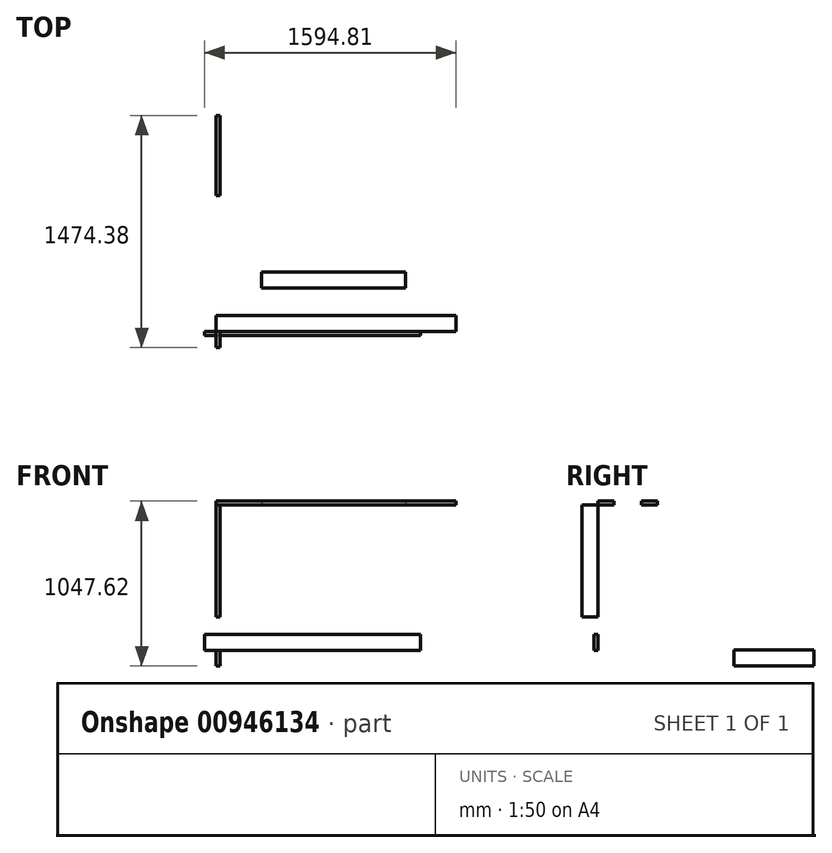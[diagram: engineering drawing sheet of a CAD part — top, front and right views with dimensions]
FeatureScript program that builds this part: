
annotation { "Feature Type Name" : "Feature", "Feature Type Description" : "" }
export const myFeature = defineFeature(function(context is Context, id is Id, definition is map)
    precondition{}
    {
        {
            var Q0;
            Q0=qCreatedBy(makeId("Top.planeOp"),FACE);
            var sketch = newSketch(context, id + "F0", { "sketchPlane" : qUnion([Q0])});
            skLineSegment(sketch, "E0.bottom", {"start": v(0, 0) * mm, "end": v(1524, 0) * mm});
            skLineSegment(sketch, "E0.top", {"start": v(0, 101.6) * mm, "end": v(1524, 101.6) * mm});
            skLineSegment(sketch, "E0.left", {"start": v(0, 0) * mm, "end": v(0, 101.6) * mm});
            skLineSegment(sketch, "E0.right", {"start": v(1524, 0) * mm, "end": v(1524, 101.6) * mm});
            skSolve(sketch);
        }
        {
            var Q0;
            Q0 = qSketchRegion(id + "F0", true);
            extrude(context, id + "F1", {"entities" : qUnion([Q0]), "depth" : 25.4 * mm, "offsetDistance" : 25.4 * mm});
        }
        {
            var Q0;
            Q0=qCreatedBy(makeId("Right.planeOp"),FACE);
            var sketch = newSketch(context, id + "F2", { "sketchPlane" : qUnion([Q0])});
            skLineSegment(sketch, "E1.bottom", {"start": v(0, 0) * mm, "end": v(-101.6, 0) * mm});
            skLineSegment(sketch, "E1.top", {"start": v(0, -711.2) * mm, "end": v(-101.6, -711.2) * mm});
            skLineSegment(sketch, "E1.left", {"start": v(0, 0) * mm, "end": v(0, -711.2) * mm});
            skLineSegment(sketch, "E1.right", {"start": v(-101.6, 0) * mm, "end": v(-101.6, -711.2) * mm});
            skSolve(sketch);
        }
        {
            var Q0;
            Q0 = qSketchRegion(id + "F2", true);
            extrude(context, id + "F3", {"entities" : qUnion([Q0]), "depth" : 25.4 * mm, "offsetDistance" : 25.4 * mm});
        }
        {
            var Q0;
            Q0=qCreatedBy(makeId("Top.planeOp"),FACE);
            var sketch = newSketch(context, id + "F4", { "sketchPlane" : qUnion([Q0])});
            skLineSegment(sketch, "E2.bottom", {"start": v(291.42, 275.85) * mm, "end": v(1205.82, 275.85) * mm});
            skLineSegment(sketch, "E2.top", {"start": v(291.42, 377.45) * mm, "end": v(1205.82, 377.45) * mm});
            skLineSegment(sketch, "E2.left", {"start": v(291.42, 275.85) * mm, "end": v(291.42, 377.45) * mm});
            skLineSegment(sketch, "E2.right", {"start": v(1205.82, 275.85) * mm, "end": v(1205.82, 377.45) * mm});
            skSolve(sketch);
        }
        {
            var Q0;
            Q0 = qSketchRegion(id + "F4", true);
            extrude(context, id + "F5", {"entities" : qUnion([Q0]), "depth" : 25.4 * mm, "offsetDistance" : 25.4 * mm});
        }
        {
            var Q0;
            Q0=qCreatedBy(makeId("Right.planeOp"),FACE);
            var sketch = newSketch(context, id + "F6", { "sketchPlane" : qUnion([Q0])});
            skLineSegment(sketch, "E3.bottom", {"start": v(864.78, -920.62) * mm, "end": v(1372.78, -920.62) * mm});
            skLineSegment(sketch, "E3.top", {"start": v(864.78, -1022.22) * mm, "end": v(1372.78, -1022.22) * mm});
            skLineSegment(sketch, "E3.left", {"start": v(864.78, -920.62) * mm, "end": v(864.78, -1022.22) * mm});
            skLineSegment(sketch, "E3.right", {"start": v(1372.78, -920.62) * mm, "end": v(1372.78, -1022.22) * mm});
            skSolve(sketch);
        }
        {
            var Q0;
            Q0 = qSketchRegion(id + "F6", true);
            extrude(context, id + "F7", {"entities" : qUnion([Q0]), "depth" : 25.4 * mm, "offsetDistance" : 25.4 * mm});
        }
        {
            var Q0;
            Q0=qCreatedBy(makeId("Front.planeOp"),FACE);
            var sketch = newSketch(context, id + "F8", { "sketchPlane" : qUnion([Q0])});
            skLineSegment(sketch, "E4.bottom", {"start": v(-70.81, -820.8) * mm, "end": v(1300.79, -820.8) * mm});
            skLineSegment(sketch, "E4.top", {"start": v(-70.81, -922.4) * mm, "end": v(1300.79, -922.4) * mm});
            skLineSegment(sketch, "E4.left", {"start": v(-70.81, -820.8) * mm, "end": v(-70.81, -922.4) * mm});
            skLineSegment(sketch, "E4.right", {"start": v(1300.79, -820.8) * mm, "end": v(1300.79, -922.4) * mm});
            skSolve(sketch);
        }
        {
            var Q0;
            Q0=makeQuery(id+"F8.imprint","IMPRINT",FACE,{"disambiguationData":[TD([[makeQuery(id+"F8.imprint","IMPRINT",EDGE,{"derivedFrom":sQuery(id+"F8.wireOp",EDGE,"E4.bottom")}),-1.0]])]});
            extrude(context, id + "F9", {"entities" : qUnion([Q0]), "depth" : 25.4 * mm, "offsetDistance" : 25.4 * mm});
        }
    });
